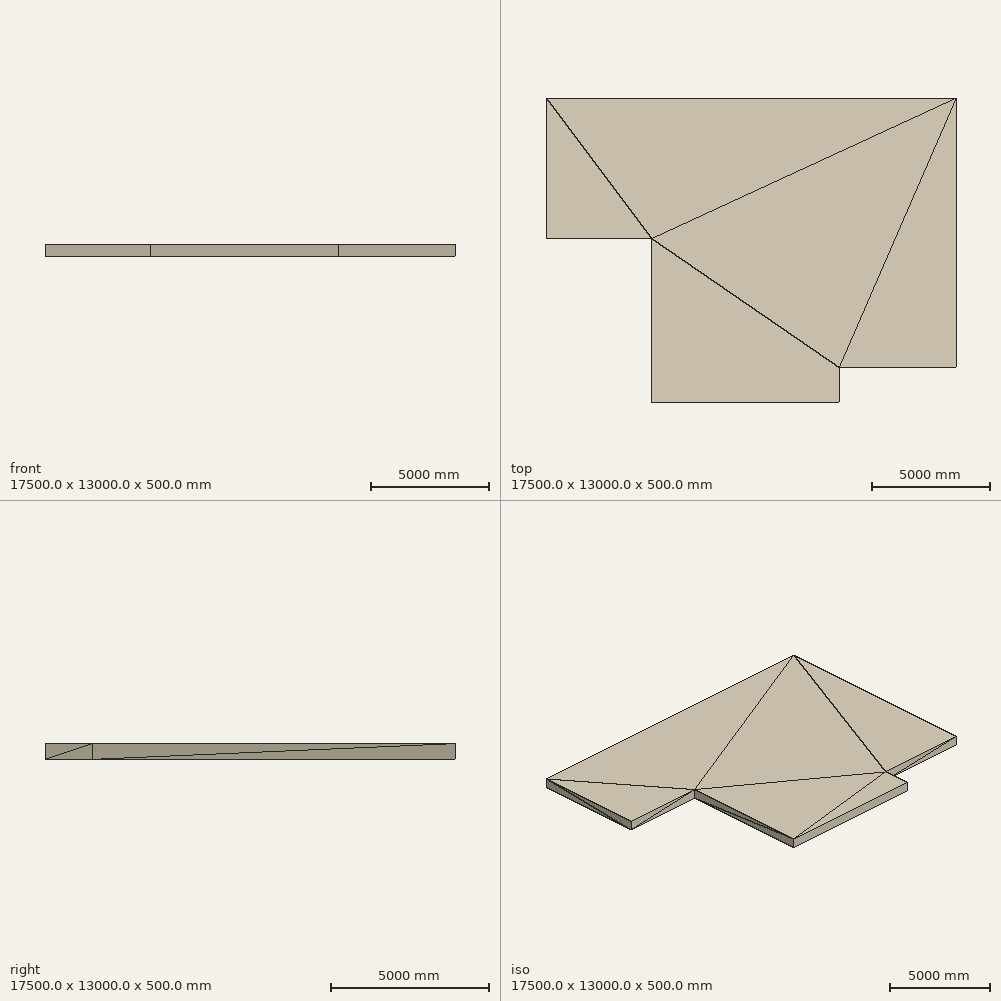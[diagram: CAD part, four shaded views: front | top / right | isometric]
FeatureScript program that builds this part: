
annotation { "Feature Type Name" : "Feature", "Feature Type Description" : "" }
export const myFeature = defineFeature(function(context is Context, id is Id, definition is map)
    precondition{}
    {
        {
            var Q0;
            Q0=qCreatedBy(makeId("Top.planeOp"),FACE);
            var sketch = newSketch(context, id + "F0", { "sketchPlane" : qUnion([Q0])});
            skLineSegment(sketch, "E0", {"start": v(0, -13132.96) * mm, "end": v(-17500, -13132.96) * mm});
            skLineSegment(sketch, "E1", {"start": v(-17500, -13132.96) * mm, "end": v(-17500, -19132.96) * mm});
            skLineSegment(sketch, "E2", {"start": v(-17500, -19132.96) * mm, "end": v(-13000, -19132.96) * mm});
            skLineSegment(sketch, "E3", {"start": v(-13000, -19132.96) * mm, "end": v(-13000, -26132.96) * mm});
            skLineSegment(sketch, "E4", {"start": v(-13000, -26132.96) * mm, "end": v(-5000, -26132.96) * mm});
            skLineSegment(sketch, "E5", {"start": v(-5000, -26132.96) * mm, "end": v(-5000, -24632.96) * mm});
            skLineSegment(sketch, "E6", {"start": v(-5000, -24632.96) * mm, "end": v(0, -24632.96) * mm});
            skLineSegment(sketch, "E7", {"start": v(0, -24632.96) * mm, "end": v(0, -13132.96) * mm});
            skSolve(sketch);
        }
        {
            var Q0;
            Q0=makeQuery(id+"F0.imprint","IMPRINT",FACE,{"disambiguationData":[TD([[makeQuery(id+"F0.imprint","IMPRINT",EDGE,{"derivedFrom":sQuery(id+"F0.wireOp",EDGE,"E0")}),1.0]])]});
            extrude(context, id + "F1", {"entities" : qUnion([Q0]), "depth" : 500 * mm, "offsetDistance" : 25 * mm});
        }
    });
